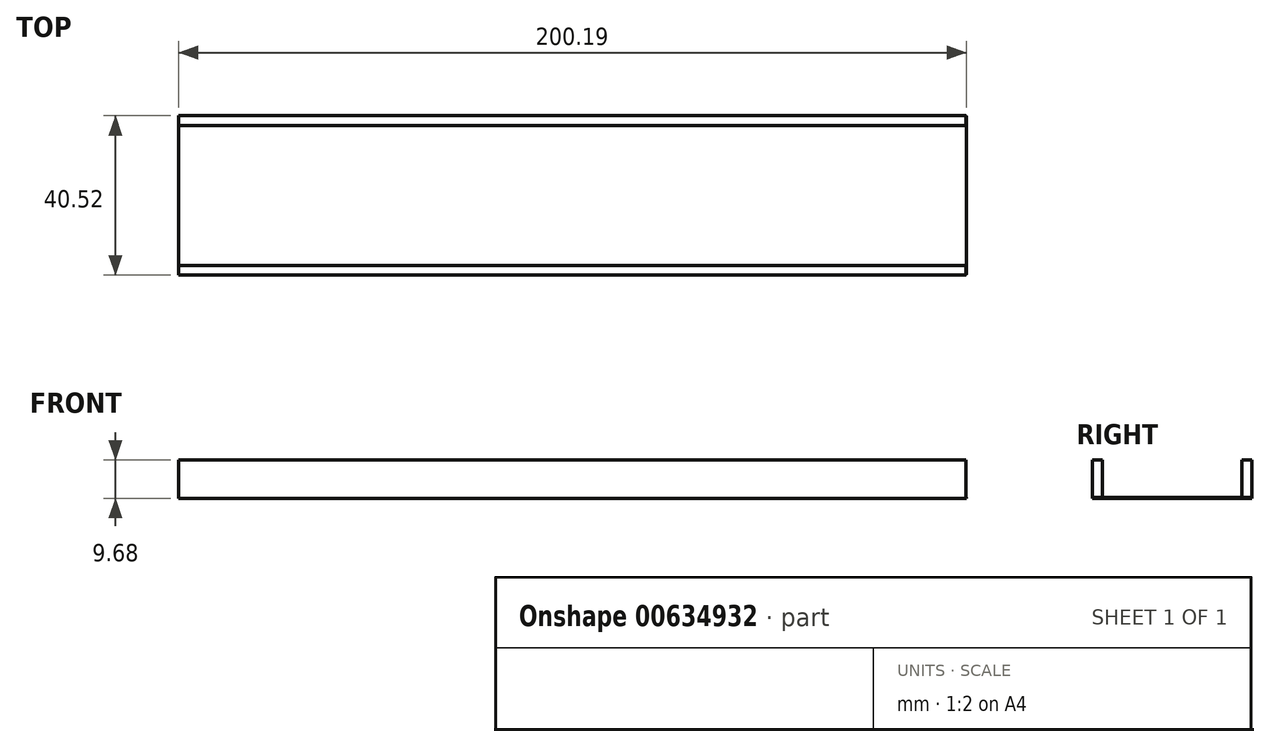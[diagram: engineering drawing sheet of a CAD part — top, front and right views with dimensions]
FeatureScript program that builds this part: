
annotation { "Feature Type Name" : "Feature", "Feature Type Description" : "" }
export const myFeature = defineFeature(function(context is Context, id is Id, definition is map)
    precondition{}
    {
        {
            var Q0;
            Q0=qCreatedBy(makeId("Top.planeOp"),FACE);
            var sketch = newSketch(context, id + "F0", { "sketchPlane" : qUnion([Q0])});
            skLineSegment(sketch, "E0.bottom", {"start": v(-100.06, 20.12) * mm, "end": v(100.06, 20.12) * mm});
            skLineSegment(sketch, "E0.top", {"start": v(-100.06, -20.12) * mm, "end": v(100.06, -20.12) * mm});
            skLineSegment(sketch, "E0.left", {"start": v(-100.06, 20.12) * mm, "end": v(-100.06, -20.12) * mm});
            skLineSegment(sketch, "E0.right", {"start": v(100.06, 20.12) * mm, "end": v(100.06, -20.12) * mm});
            skPoint(sketch, "E0.middle", {"position": v(0, 0) * mm});
            skSolve(sketch);
        }
        {
            var Q0;
            Q0=qCreatedBy(makeId("Top.planeOp"),FACE);
            var sketch = newSketch(context, id + "F1", { "sketchPlane" : qUnion([Q0])});
            skLineSegment(sketch, "E1.bottom", {"start": v(-100.13, 20.26) * mm, "end": v(100.01, 20.26) * mm});
            skLineSegment(sketch, "E1.top", {"start": v(-100.13, 17.76) * mm, "end": v(100.01, 17.76) * mm});
            skLineSegment(sketch, "E1.left", {"start": v(-100.13, 20.26) * mm, "end": v(-100.13, 17.76) * mm});
            skLineSegment(sketch, "E1.right", {"start": v(100.01, 20.26) * mm, "end": v(100.01, 17.76) * mm});
            skSolve(sketch);
        }
        {
            var Q0;
            Q0 = qSketchRegion(id + "FD4dhX6xmup0Ml7_0", true);
            var Q1;
            Q1 = qSketchRegion(id + "F1", true);
            extrude(context, id + "F2", {"entities" : qUnion([Q0, Q1]), "depth" : 9.68 * mm, "offsetDistance" : 25.4 * mm});
        }
        {
            var Q0;
            Q0 = qSketchRegion(id + "F0", true);
            extrude(context, id + "F3", {"entities" : qUnion([Q0]), "depth" : 0.25 * mm, "offsetDistance" : 25.4 * mm});
        }
        {
            var Q0;
            Q0=makeQuery(id+"F2.opExtrude","SWEPT_BODY",BODY,{"disambiguationData":[OSD([sQuery(id+"F1.wireOp",EDGE,"E1.bottom"),sQuery(id+"F1.wireOp",EDGE,"E1.top"),sQuery(id+"F1.wireOp",EDGE,"E1.left"),sQuery(id+"F1.wireOp",EDGE,"E1.right")])]});
            var Q1;
            Q1=qCreatedBy(makeId("Front.planeOp"),FACE);
            mirror(context, id + "F4", {"entities" : qUnion([Q0]), "mirrorPlane" : qUnion([Q1])});
        }
    });
